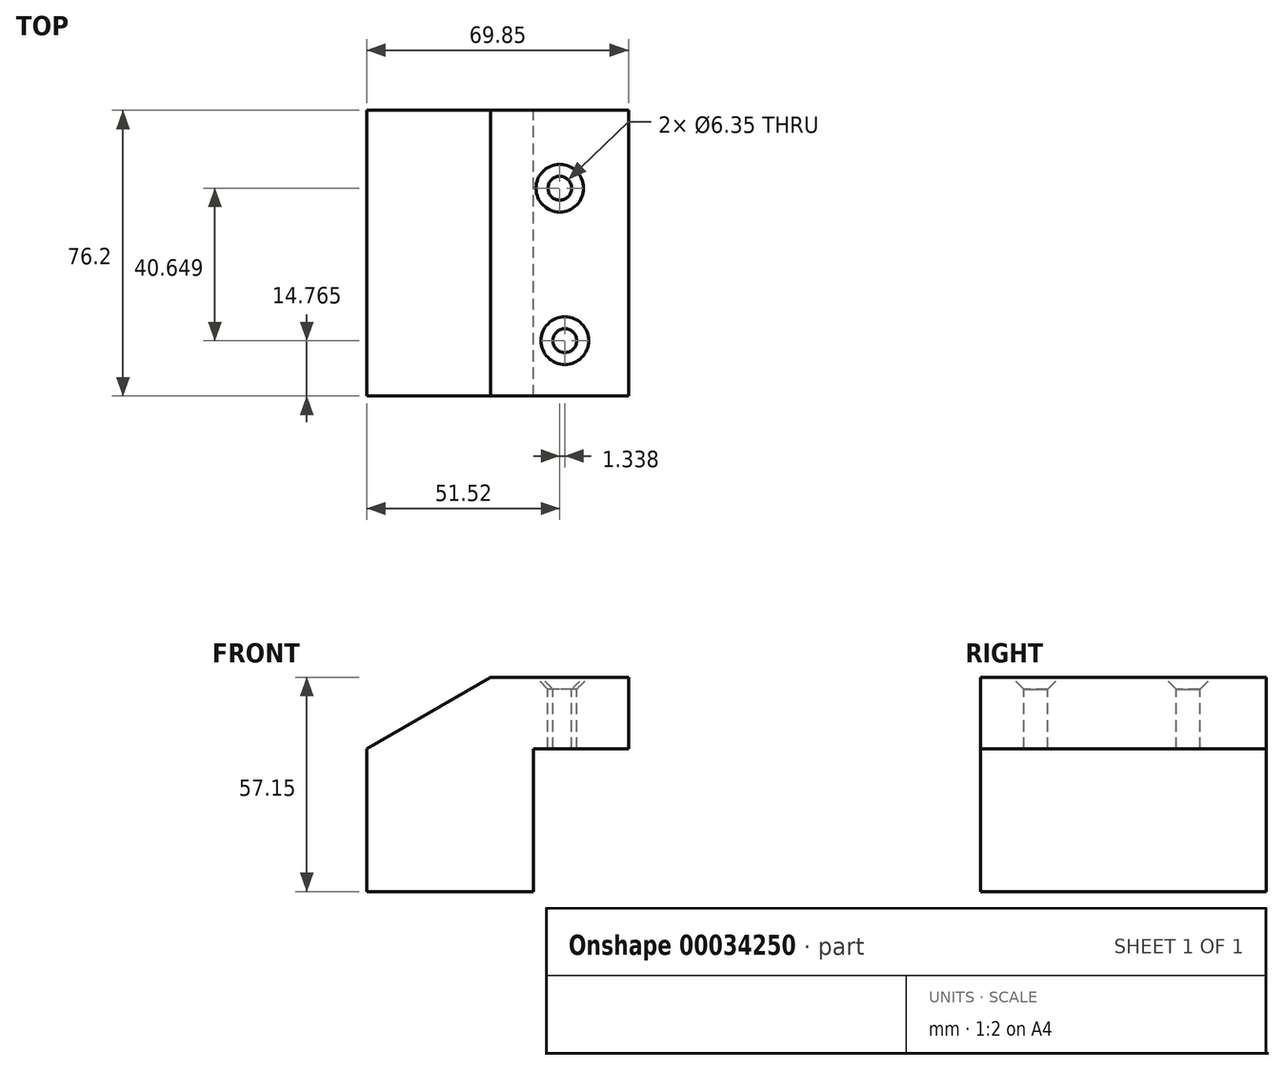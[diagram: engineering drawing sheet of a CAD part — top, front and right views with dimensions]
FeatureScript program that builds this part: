
annotation { "Feature Type Name" : "Feature", "Feature Type Description" : "" }
export const myFeature = defineFeature(function(context is Context, id is Id, definition is map)
    precondition{}
    {
        {
            var Q0;
            Q0=qCreatedBy(makeId("Front.planeOp"),FACE);
            var sketch = newSketch(context, id + "F0", { "sketchPlane" : qUnion([Q0])});
            skLineSegment(sketch, "E0.bottom", {"start": v(0, 0) * mm, "end": v(-44.45, 0) * mm});
            skLineSegment(sketch, "E0.left", {"start": v(0, 0) * mm, "end": v(0, 38.1) * mm});
            skLineSegment(sketch, "E0.right", {"start": v(-44.45, 0) * mm, "end": v(-44.45, 38.1) * mm});
            skLineSegment(sketch, "E1", {"start": v(-44.45, 38.1) * mm, "end": v(-11.45, 57.15) * mm});
            skLineSegment(sketch, "E2", {"start": v(-11.45, 57.15) * mm, "end": v(25.4, 57.15) * mm});
            skLineSegment(sketch, "E3", {"start": v(25.4, 57.15) * mm, "end": v(25.4, 38.1) * mm});
            skLineSegment(sketch, "E4", {"start": v(25.4, 38.1) * mm, "end": v(0, 38.1) * mm});
            skSolve(sketch);
        }
        {
            var Q0;
            Q0=makeQuery(id+"F0.imprint","IMPRINT",FACE,{"disambiguationData":[TD([[makeQuery(id+"F0.imprint","IMPRINT",EDGE,{"derivedFrom":sQuery(id+"F0.wireOp",EDGE,"E0.bottom")}),-1.0]])]});
            extrude(context, id + "F1", {"entities" : qUnion([Q0]), "depth" : 76.2 * mm});
        }
        {
            var Q0;
            Q0=makeQuery(id+"F1.opExtrude","SWEPT_FACE",FACE,{"disambiguationData":[OSD([sQuery(id+"F0.wireOp",EDGE,"E2")])]});
            var sketch = newSketch(context, id + "F2", { "sketchPlane" : qUnion([Q0])});
            skPoint(sketch, "E5", {"position": v(8.4, -61.44) * mm});
            skPoint(sketch, "E6", {"position": v(7.07, -20.79) * mm});
            skSolve(sketch);
        }
        {
            var Q0;
            Q0=sQuery(id+"F2.wireOp",VERTEX,"E5");
            var Q1;
            Q1=sQuery(id+"F2.wireOp",VERTEX,"E6");
            var Q2;
            Q2=makeQuery(id+"F1.opExtrude","SWEPT_BODY",BODY,{"disambiguationData":[OSD([sQuery(id+"F0.wireOp",EDGE,"E0.bottom"),sQuery(id+"F0.wireOp",EDGE,"E0.left"),sQuery(id+"F0.wireOp",EDGE,"E0.right"),sQuery(id+"F0.wireOp",EDGE,"E1"),sQuery(id+"F0.wireOp",EDGE,"E2"),sQuery(id+"F0.wireOp",EDGE,"E3"),sQuery(id+"F0.wireOp",EDGE,"E4")])]});
            hole(context, id + "F3", {"style" : HoleStyle.C_SINK, "holeDiameter" : 6.35 * mm, "cSinkDiameter" : 12.7 * mm, "endStyle" : HoleEndStyle.THROUGH, "locations" : qUnion([Q0, Q1]), "scope" : qUnion([Q2]), "cSinkAngle" : 90 * degree});
        }
    });
